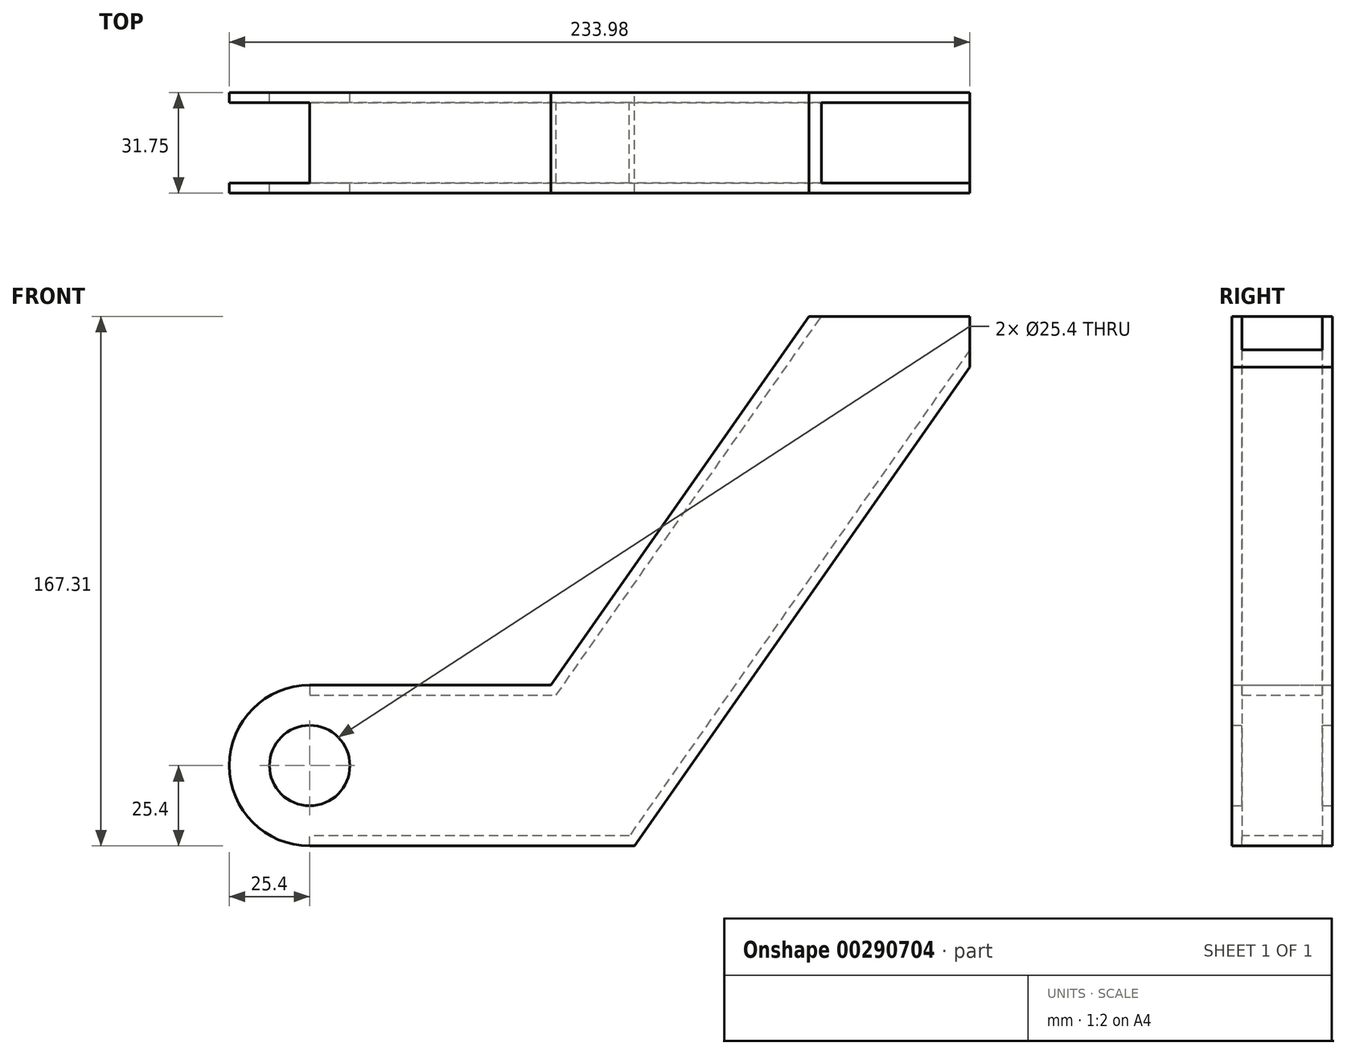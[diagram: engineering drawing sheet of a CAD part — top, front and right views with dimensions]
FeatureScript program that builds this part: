
annotation { "Feature Type Name" : "Feature", "Feature Type Description" : "" }
export const myFeature = defineFeature(function(context is Context, id is Id, definition is map)
    precondition{}
    {
        {
            var Q0;
            Q0=qCreatedBy(makeId("Front.planeOp"),FACE);
            var sketch = newSketch(context, id + "F0", { "sketchPlane" : qUnion([Q0])});
            skLineSegment(sketch, "E0", {"start": v(25.4, 0) * mm, "end": v(101.6, 0) * mm});
            skLineSegment(sketch, "E1", {"start": v(101.6, 0) * mm, "end": v(203.58, 145.65) * mm});
            skLineSegment(sketch, "E2", {"start": v(203.58, 145.65) * mm, "end": v(245.2, 116.5) * mm});
            skLineSegment(sketch, "E3", {"start": v(245.2, 116.5) * mm, "end": v(128.04, -50.8) * mm});
            skLineSegment(sketch, "E4", {"start": v(128.04, -50.8) * mm, "end": v(25.4, -50.8) * mm});
            skLineSegment(sketch, "E5", {"start": v(0, -25.4) * mm, "end": v(0, -25.4) * mm});
            skCircle(sketch, "E6", {"center": v(25.4, -25.4) * mm, "radius": 12.7 * mm});
            skPoint(sketch, "E6.centerSnap0", {"position": v(0, -25.4) * mm});
            skPoint(sketch, "E7.visualSharp", {"position": v(0, 0) * mm});
            skArc(sketch, "E7.filletArc", {"start": v(25.4, 0) * mm, "mid": v(7.44, -7.44) * mm, "end": v(0, -25.4) * mm});
            skPoint(sketch, "E8.visualSharp", {"position": v(0, -50.8) * mm});
            skArc(sketch, "E8.filletArc", {"start": v(0, -25.4) * mm, "mid": v(7.44, -43.36) * mm, "end": v(25.4, -50.8) * mm});
            skLineSegment(sketch, "E9", {"start": v(245.2, 116.5) * mm, "end": v(183.18, 116.5) * mm});
            skLineSegment(sketch, "E10", {"start": v(233.98, 116.5) * mm, "end": v(233.98, 100.5) * mm});
            skSolve(sketch);
        }
        {
            var Q0;
            Q0=makeQuery(id+"F0.imprint","IMPRINT",FACE,{"disambiguationData":[TD([[makeQuery(id+"F0.imprint","IMPRINT",EDGE,{"derivedFrom":sQuery(id+"F0.wireOp",EDGE,"E0")}),-1.0]])]});
            extrude(context, id + "F1", {"entities" : qUnion([Q0]), "depth" : 31.75 * mm});
        }
        {
            var Q0;
            Q0=makeQuery(id+"F1.opExtrude","SWEPT_FACE",FACE,{"disambiguationData":[OSD([sQuery(id+"F0.wireOp",EDGE,"E9")])]});
            var Q1;
            Q1=makeQuery(id+"F1.opExtrude","SWEPT_FACE",FACE,{"disambiguationData":[OSD([sQuery(id+"F0.wireOp",EDGE,"E6")])]});
            var Q2;
            Q2=makeQuery(id+"F1.opExtrude","SWEPT_FACE",FACE,{"disambiguationData":[OSD([sQuery(id+"F0.wireOp",EDGE,"E7.filletArc"),sQuery(id+"F0.wireOp",EDGE,"E8.filletArc")])]});
            var Q3;
            Q3=makeQuery(id+"F1.opExtrude","SWEPT_FACE",FACE,{"disambiguationData":[OSD([sQuery(id+"F0.wireOp",EDGE,"E10")])]});
            shell(context, id + "F2", {"entities" : qUnion([Q0, Q1, Q2, Q3]), "thickness" : 3.17 * mm});
        }
    });
